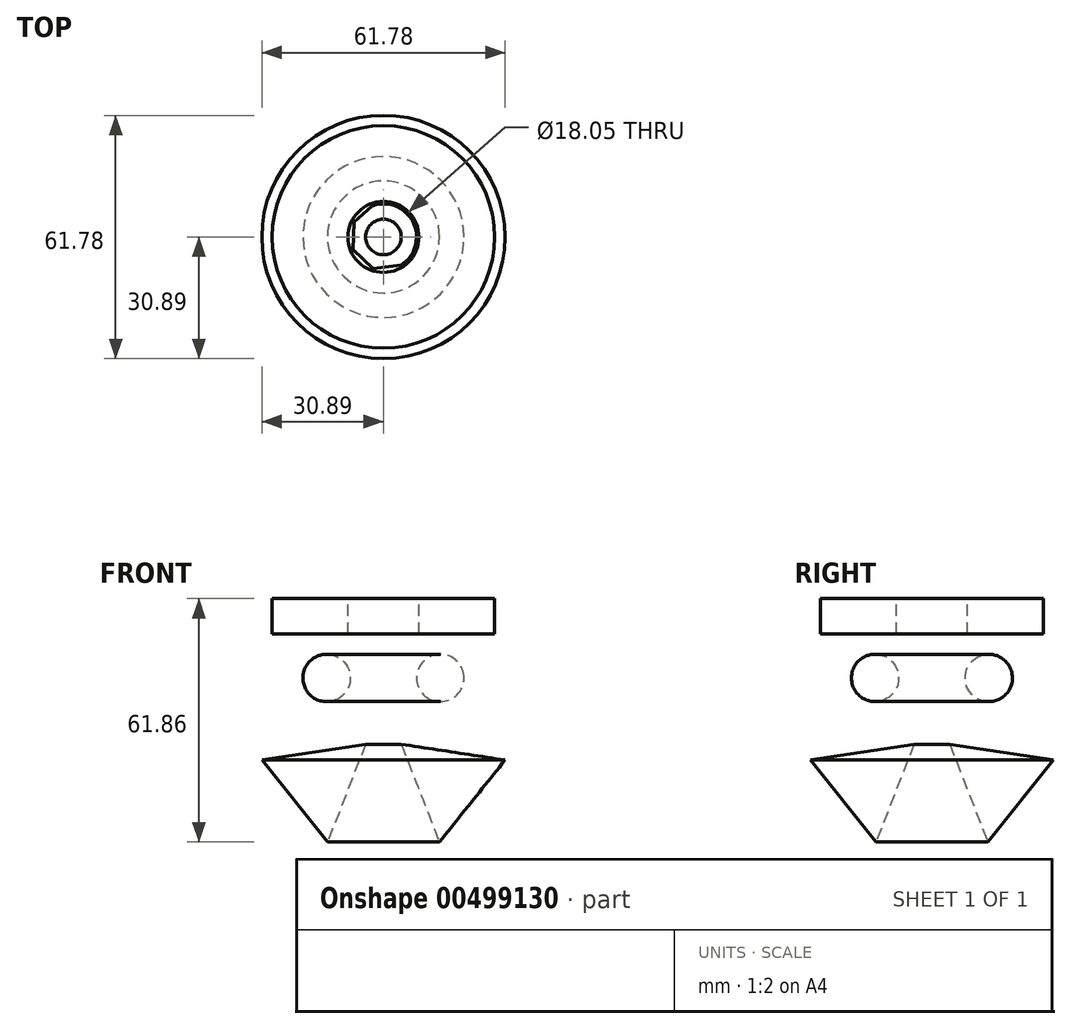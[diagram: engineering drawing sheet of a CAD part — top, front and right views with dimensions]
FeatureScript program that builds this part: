
annotation { "Feature Type Name" : "Feature", "Feature Type Description" : "" }
export const myFeature = defineFeature(function(context is Context, id is Id, definition is map)
    precondition{}
    {
        {
            var Q0;
            Q0=qCreatedBy(makeId("Front.planeOp"),FACE);
            var sketch = newSketch(context, id + "F0", { "sketchPlane" : qUnion([Q0])});
            skLineSegment(sketch, "E0", {"start": v(0, 75.2) * mm, "end": v(0, 0) * mm, "construction": true});
            skLineSegment(sketch, "E1.bottom", {"start": v(9.02, 67.98) * mm, "end": v(28.27, 67.98) * mm});
            skLineSegment(sketch, "E1.top", {"start": v(9.02, 58.95) * mm, "end": v(28.27, 58.95) * mm});
            skLineSegment(sketch, "E1.left", {"start": v(9.02, 67.98) * mm, "end": v(9.02, 58.95) * mm});
            skLineSegment(sketch, "E1.right", {"start": v(28.27, 67.98) * mm, "end": v(28.27, 58.95) * mm});
            skCircle(sketch, "E2", {"center": v(14.44, 47.83) * mm, "radius": 6.02 * mm});
            skCircle(sketch, "E3.cCircle", {"center": v(16.54, 21.36) * mm, "radius": 7.7 * mm, "construction": true});
            skLineSegment(sketch, "E3.0", {"start": v(30.9, 26.96) * mm, "end": v(14.22, 6.12) * mm});
            skLineSegment(sketch, "E3.1", {"start": v(14.22, 6.12) * mm, "end": v(4.51, 30.98) * mm});
            skLineSegment(sketch, "E3.2", {"start": v(4.51, 30.98) * mm, "end": v(30.9, 26.96) * mm});
            skPoint(sketch, "E3.0.midPoint", {"position": v(22.56, 16.54) * mm});
            skSolve(sketch);
        }
        {
            var Q0;
            Q0 = qSketchRegion(id + "F0", true);
            var Q1;
            Q1=sQuery(id+"F0.wireOp",EDGE,"E0");
            revolve(context, id + "F1", {"entities" : qUnion([Q0]), "axis" : qUnion([Q1]), "revolveType" : RevolveType.FULL});
        }
    });
